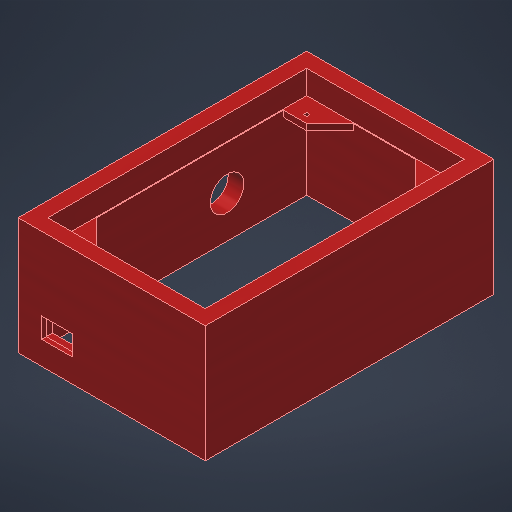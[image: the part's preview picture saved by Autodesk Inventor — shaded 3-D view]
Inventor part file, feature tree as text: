
AUTODESK INVENTOR PART (.ipt)
format: ipt  version: 2025.2 (Build 292293000, 293)  size: 316,928 bytes
history: native  units: in
note: dims shown in document units (in); Inventor stores cm internally (conversion verified against a paired STEP export)
features: extrude x10, sketch x5, plane x1
ambient origin geometry x8: Origin, YZ Plane, XZ Plane, XY Plane, X Axis, Y Axis, Z Axis, Center Point
bodies: Solid1 (feature_tree)
feature tree (16):
  extrude  "Extrusion1"  Depth=6.4961in
  plane  "Work Plane2"
  extrude  "Extrusion3"  Depth=7.2835in
  extrude  "Extrusion5"  [1 undecoded]
  extrude  "Extrusion8"  Depth=1.1811in
  extrude  "Extrusion9"  Depth=0.3937in
  extrude  "Extrusion10"  Depth=0.1575in TaperAngle=0.0deg
  extrude  "Extrusion11"  Depth=0.3937in
  extrude  "Extrusion12"  Depth=0.3937in
  extrude  "Extrusion13"  Depth=0.3937in
  extrude  "Extrusion14"  Depth=0.3937in
  sketch  "Sketch11"  dims[d0=3.937in d1=6.4961in]
  sketch  "Sketch15"  dims[d2=4.7244in d3=7.2835in]
  sketch  "Sketch16"  dims[d4=2.9528in d5=0.0in d8=-0.5984in]
  sketch  "Sketch18"  dims[d9=1.1811in d10=1.1811in]
  sketch  "Sketch19"  dims[d11=0.1575in d12=0.0in d17=0.1024in d18=0.1575in d19=0.0in d20=1.1811in d21=0.3937in d22=0.3937in d23=0.1024in d24=0.3937in d25=0.3937in d26=0.1024in d27=0.3937in d28=0.3937in d29=0.1024in d38=4.3307in d39=6.8898in d40=0.1969in d41=0.0in d42=0.0591in d43=0.0591in d44=0.0591in d45=0.0591in d46=0.1969in d47=0.0in d48=0.3937in d49=0.3937in d50=1.1811in d51=3.9764in d52=6.5354in d53=0.5984in d54=0.0in d56=0.5906in d57=0.5906in d58=0.5906in d59=0.1575in d60=0.0in d61=0.5906in d62=0.5906in d63=0.7717in d64=0.5118in d65=0.3937in d66=0.0in d67=0.1181in d68=0.1181in d69=0.1181in d70=0.1181in d71=0.2756in d72=0.0in d73=2.0079in d74=1.0433in d75=0.8465in d76=0.3937in d77=0.0in]
note: 1 required parameter value undecoded (feature->parameter linkage not recoverable at this tier; creation-order binding heuristic only, values carry confidence <= 0.55)
